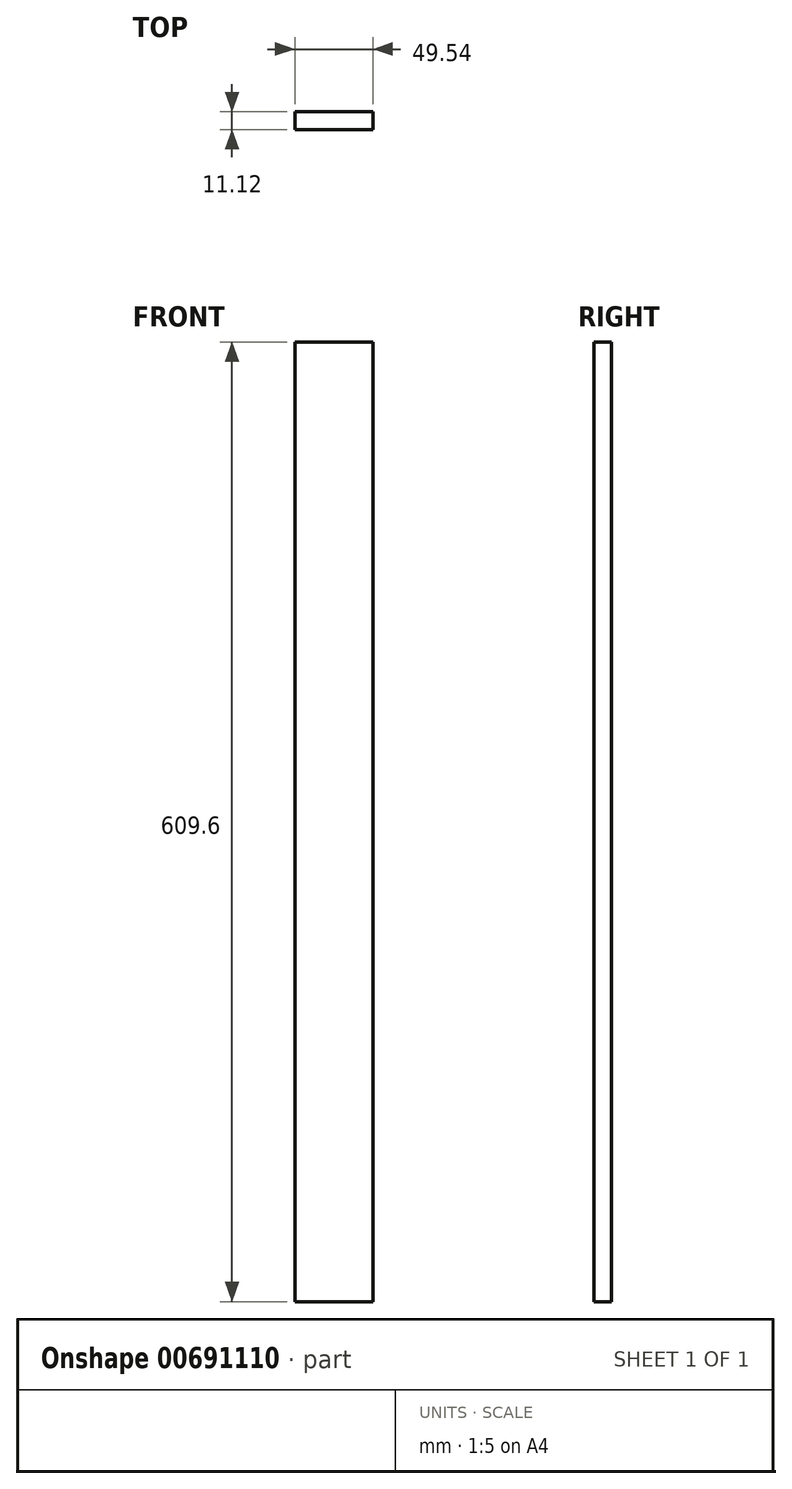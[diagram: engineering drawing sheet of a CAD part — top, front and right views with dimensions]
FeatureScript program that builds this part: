
annotation { "Feature Type Name" : "Feature", "Feature Type Description" : "" }
export const myFeature = defineFeature(function(context is Context, id is Id, definition is map)
    precondition{}
    {
        {
            var Q0;
            Q0=qCreatedBy(makeId("Top.planeOp"),FACE);
            var sketch = newSketch(context, id + "F0", { "sketchPlane" : qUnion([Q0])});
            skLineSegment(sketch, "E0.bottom", {"start": v(24.77, -5.56) * mm, "end": v(-24.77, -5.56) * mm});
            skLineSegment(sketch, "E0.top", {"start": v(24.77, 5.56) * mm, "end": v(-24.77, 5.56) * mm});
            skLineSegment(sketch, "E0.left", {"start": v(24.77, -5.56) * mm, "end": v(24.77, 5.56) * mm});
            skLineSegment(sketch, "E0.right", {"start": v(-24.77, -5.56) * mm, "end": v(-24.77, 5.56) * mm});
            skPoint(sketch, "E0.middle", {"position": v(0, 0) * mm});
            skSolve(sketch);
        }
        {
            var Q0;
            Q0 = qSketchRegion(id + "F0", true);
            extrude(context, id + "F1", {"entities" : qUnion([Q0]), "depth" : 609.6 * mm, "offsetDistance" : 25.4 * mm});
        }
    });
